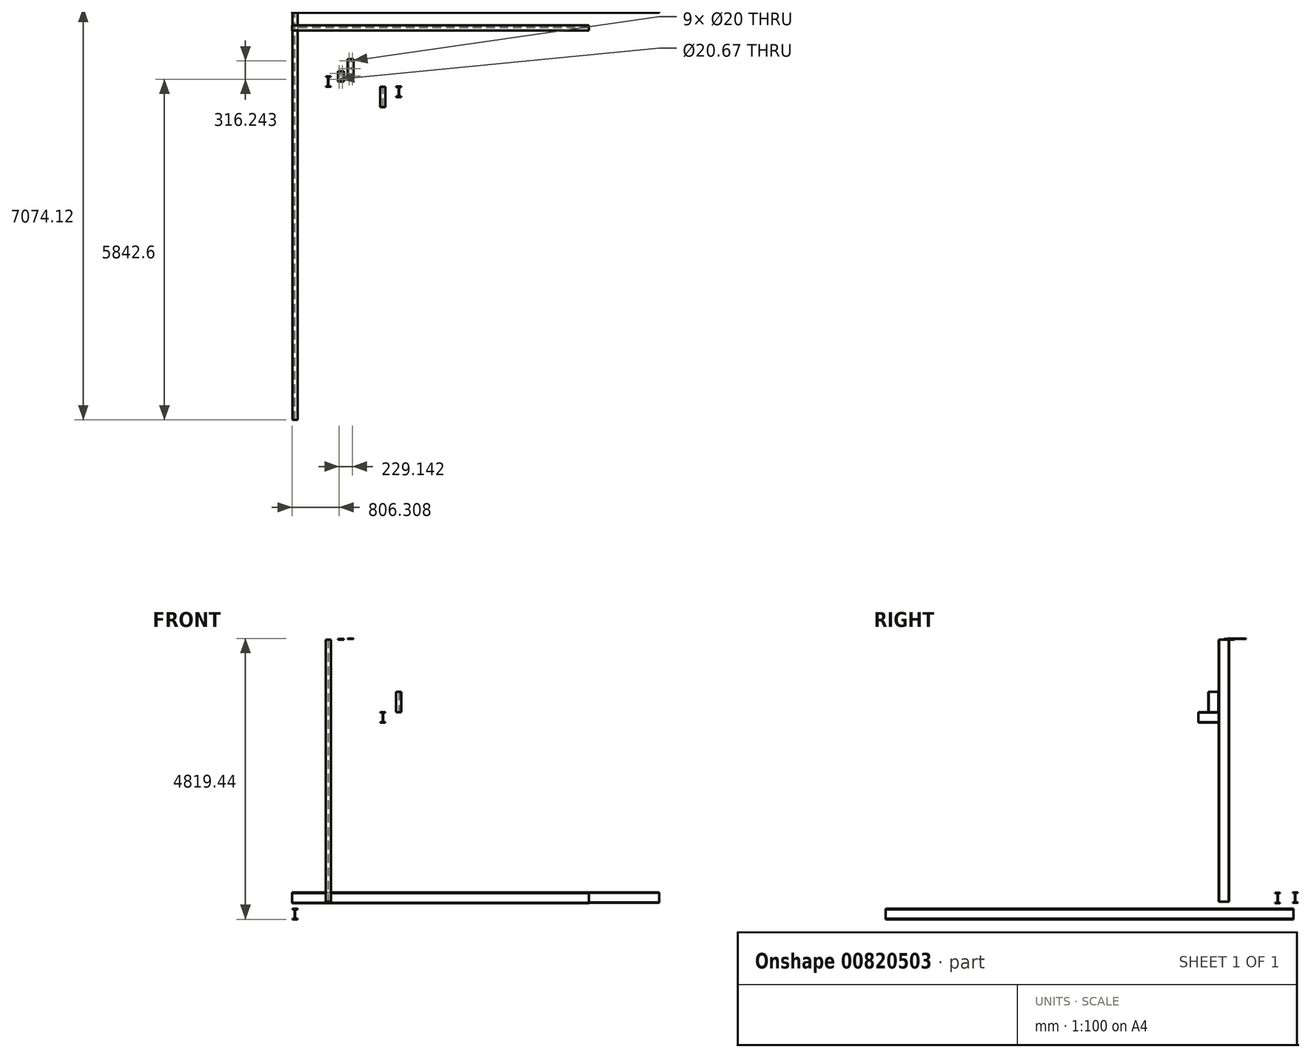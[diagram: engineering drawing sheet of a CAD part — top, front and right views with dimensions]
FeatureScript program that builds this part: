
annotation { "Feature Type Name" : "Feature", "Feature Type Description" : "" }
export const myFeature = defineFeature(function(context is Context, id is Id, definition is map)
    precondition{}
    {
        {
            var Q0;
            Q0=qCreatedBy(makeId("Right.planeOp"),FACE);
            var sketch = newSketch(context, id + "F0", { "sketchPlane" : qUnion([Q0])});
            skLineSegment(sketch, "E0", {"start": v(74.12, -15.88) * mm, "end": v(-15.88, -15.88) * mm});
            skLineSegment(sketch, "E1", {"start": v(-15.88, -15.88) * mm, "end": v(-15.88, -7.88) * mm});
            skLineSegment(sketch, "E2", {"start": v(-15.88, -7.88) * mm, "end": v(26.12, -7.88) * mm});
            skLineSegment(sketch, "E3", {"start": v(26.12, -7.88) * mm, "end": v(26.12, 156.12) * mm});
            skLineSegment(sketch, "E4", {"start": v(26.12, 156.12) * mm, "end": v(-15.88, 156.12) * mm});
            skLineSegment(sketch, "E5", {"start": v(-15.88, 156.12) * mm, "end": v(-15.88, 164.12) * mm});
            skLineSegment(sketch, "E6", {"start": v(-15.88, 164.12) * mm, "end": v(74.12, 164.12) * mm});
            skLineSegment(sketch, "E7", {"start": v(74.12, 164.12) * mm, "end": v(74.12, 156.12) * mm});
            skLineSegment(sketch, "E8", {"start": v(74.12, 156.12) * mm, "end": v(32.12, 156.12) * mm});
            skLineSegment(sketch, "E9", {"start": v(32.12, 156.12) * mm, "end": v(32.12, -7.88) * mm});
            skLineSegment(sketch, "E10", {"start": v(32.12, -7.88) * mm, "end": v(74.12, -7.88) * mm});
            skLineSegment(sketch, "E11", {"start": v(74.12, -7.88) * mm, "end": v(74.12, -15.88) * mm});
            skSolve(sketch);
        }
        {
            var Q0;
            Q0=makeQuery(id+"F0.imprint","IMPRINT",FACE,{"disambiguationData":[TD([[makeQuery(id+"F0.imprint","IMPRINT",EDGE,{"derivedFrom":sQuery(id+"F0.wireOp",EDGE,"E0")}),-1.0]])]});
            extrude(context, id + "F1", {"entities" : qUnion([Q0]), "depth" : 6300 * mm, "offsetDistance" : 25 * mm});
        }
        {
            var Q0;
            Q0=qCreatedBy(makeId("Front.planeOp"),FACE);
            var sketch = newSketch(context, id + "F2", { "sketchPlane" : qUnion([Q0])});
            skLineSegment(sketch, "E12", {"start": v(5.31, -299.44) * mm, "end": v(95.31, -299.44) * mm});
            skLineSegment(sketch, "E13", {"start": v(95.31, -299.44) * mm, "end": v(95.31, -291.44) * mm});
            skLineSegment(sketch, "E14", {"start": v(95.31, -291.44) * mm, "end": v(53.31, -291.44) * mm});
            skLineSegment(sketch, "E15", {"start": v(53.31, -291.44) * mm, "end": v(53.31, -127.44) * mm});
            skLineSegment(sketch, "E16", {"start": v(53.31, -127.44) * mm, "end": v(95.31, -127.44) * mm});
            skLineSegment(sketch, "E17", {"start": v(95.31, -127.44) * mm, "end": v(95.31, -119.44) * mm});
            skLineSegment(sketch, "E18", {"start": v(95.31, -119.44) * mm, "end": v(5.31, -119.44) * mm});
            skLineSegment(sketch, "E19", {"start": v(5.31, -119.44) * mm, "end": v(5.31, -127.44) * mm});
            skLineSegment(sketch, "E20", {"start": v(5.31, -127.44) * mm, "end": v(47.31, -127.44) * mm});
            skLineSegment(sketch, "E21", {"start": v(47.31, -127.44) * mm, "end": v(47.31, -291.44) * mm});
            skLineSegment(sketch, "E22", {"start": v(47.31, -291.44) * mm, "end": v(5.31, -291.44) * mm});
            skLineSegment(sketch, "E23", {"start": v(5.31, -291.44) * mm, "end": v(5.31, -299.44) * mm});
            skSolve(sketch);
        }
        {
            var Q0;
            Q0=makeQuery(id+"F2.imprint","IMPRINT",FACE,{"disambiguationData":[TD([[makeQuery(id+"F2.imprint","IMPRINT",EDGE,{"derivedFrom":sQuery(id+"F2.wireOp",EDGE,"E12")}),1.0]])]});
            extrude(context, id + "F3", {"entities" : qUnion([Q0]), "depth" : 7000 * mm, "offsetDistance" : 25 * mm});
        }
        {
            var Q0;
            Q0=qCreatedBy(makeId("Right.planeOp"),FACE);
            var sketch = newSketch(context, id + "F4", { "sketchPlane" : qUnion([Q0])});
            skLineSegment(sketch, "E24", {"start": v(-227.32, -23.27) * mm, "end": v(-317.32, -23.27) * mm});
            skLineSegment(sketch, "E25", {"start": v(-317.32, -23.27) * mm, "end": v(-317.32, -15.27) * mm});
            skLineSegment(sketch, "E26", {"start": v(-317.32, -15.27) * mm, "end": v(-275.32, -15.27) * mm});
            skLineSegment(sketch, "E27", {"start": v(-275.32, -15.27) * mm, "end": v(-275.32, 148.73) * mm});
            skLineSegment(sketch, "E28", {"start": v(-275.32, 148.73) * mm, "end": v(-317.32, 148.73) * mm});
            skLineSegment(sketch, "E29", {"start": v(-317.32, 148.73) * mm, "end": v(-317.32, 156.73) * mm});
            skLineSegment(sketch, "E30", {"start": v(-317.32, 156.73) * mm, "end": v(-227.32, 156.73) * mm});
            skLineSegment(sketch, "E31", {"start": v(-227.32, 156.73) * mm, "end": v(-227.32, 148.73) * mm});
            skLineSegment(sketch, "E32", {"start": v(-227.32, 148.73) * mm, "end": v(-269.32, 148.73) * mm});
            skLineSegment(sketch, "E33", {"start": v(-269.32, 148.73) * mm, "end": v(-269.32, -15.27) * mm});
            skLineSegment(sketch, "E34", {"start": v(-269.32, -15.27) * mm, "end": v(-227.32, -15.27) * mm});
            skLineSegment(sketch, "E35", {"start": v(-227.32, -15.27) * mm, "end": v(-227.32, -23.27) * mm});
            skSolve(sketch);
        }
        {
            var Q0;
            Q0=makeQuery(id+"F4.imprint","IMPRINT",FACE,{"disambiguationData":[TD([[makeQuery(id+"F4.imprint","IMPRINT",EDGE,{"derivedFrom":sQuery(id+"F4.wireOp",EDGE,"E24")}),-1.0]])]});
            extrude(context, id + "F5", {"entities" : qUnion([Q0]), "depth" : 5090 * mm, "offsetDistance" : 25 * mm});
        }
        {
            var Q0;
            Q0=qCreatedBy(makeId("Top.planeOp"),FACE);
            var sketch = newSketch(context, id + "F6", { "sketchPlane" : qUnion([Q0])});
            skLineSegment(sketch, "E36", {"start": v(574.81, -1284.27) * mm, "end": v(664.81, -1284.27) * mm});
            skLineSegment(sketch, "E37", {"start": v(664.81, -1284.27) * mm, "end": v(664.81, -1276.27) * mm});
            skLineSegment(sketch, "E38", {"start": v(664.81, -1276.27) * mm, "end": v(622.81, -1276.27) * mm});
            skLineSegment(sketch, "E39", {"start": v(622.81, -1276.27) * mm, "end": v(622.81, -1112.27) * mm});
            skLineSegment(sketch, "E40", {"start": v(622.81, -1112.27) * mm, "end": v(664.81, -1112.27) * mm});
            skLineSegment(sketch, "E41", {"start": v(664.81, -1112.27) * mm, "end": v(664.81, -1104.27) * mm});
            skLineSegment(sketch, "E42", {"start": v(664.81, -1104.27) * mm, "end": v(574.81, -1104.27) * mm});
            skLineSegment(sketch, "E43", {"start": v(574.81, -1104.27) * mm, "end": v(574.81, -1112.27) * mm});
            skLineSegment(sketch, "E44", {"start": v(574.81, -1112.27) * mm, "end": v(616.81, -1112.27) * mm});
            skLineSegment(sketch, "E45", {"start": v(616.81, -1112.27) * mm, "end": v(616.81, -1276.27) * mm});
            skLineSegment(sketch, "E46", {"start": v(616.81, -1276.27) * mm, "end": v(574.81, -1276.27) * mm});
            skLineSegment(sketch, "E47", {"start": v(574.81, -1276.27) * mm, "end": v(574.81, -1284.27) * mm});
            skSolve(sketch);
        }
        {
            var Q0;
            Q0=makeQuery(id+"F6.imprint","IMPRINT",FACE,{"disambiguationData":[TD([[makeQuery(id+"F6.imprint","IMPRINT",EDGE,{"derivedFrom":sQuery(id+"F6.wireOp",EDGE,"E36")}),1.0]])]});
            extrude(context, id + "F7", {"entities" : qUnion([Q0]), "depth" : 4500 * mm, "offsetDistance" : 25 * mm});
        }
        {
            var Q0;
            Q0=makeQuery(id+"F7.opExtrude","CAP_FACE",FACE,{"disambiguationData":[OSD([sQuery(id+"F6.wireOp",EDGE,"E36"),sQuery(id+"F6.wireOp",EDGE,"E37"),sQuery(id+"F6.wireOp",EDGE,"E38"),sQuery(id+"F6.wireOp",EDGE,"E39"),sQuery(id+"F6.wireOp",EDGE,"E40"),sQuery(id+"F6.wireOp",EDGE,"E41"),sQuery(id+"F6.wireOp",EDGE,"E42"),sQuery(id+"F6.wireOp",EDGE,"E43"),sQuery(id+"F6.wireOp",EDGE,"E44"),sQuery(id+"F6.wireOp",EDGE,"E45"),sQuery(id+"F6.wireOp",EDGE,"E46"),sQuery(id+"F6.wireOp",EDGE,"E47")])],"isStart":false});
            var sketch = newSketch(context, id + "F8", { "sketchPlane" : qUnion([Q0])});
            skLineSegment(sketch, "E48.bottom", {"start": v(886.3, -1197.4) * mm, "end": v(786.3, -1197.4) * mm});
            skLineSegment(sketch, "E48.top", {"start": v(886.3, -1017.4) * mm, "end": v(786.3, -1017.4) * mm});
            skLineSegment(sketch, "E48.left", {"start": v(886.3, -1197.4) * mm, "end": v(886.3, -1017.4) * mm});
            skLineSegment(sketch, "E48.right", {"start": v(786.3, -1197.4) * mm, "end": v(786.3, -1017.4) * mm});
            skPoint(sketch, "E48.middle", {"position": v(836.3, -1107.4) * mm});
            skCircle(sketch, "E49", {"center": v(866.3, -1057.4) * mm, "radius": 10 * mm});
            skCircle(sketch, "E50", {"center": v(866.3, -1157.4) * mm, "radius": 10 * mm});
            skCircle(sketch, "E51", {"center": v(806.3, -1057.4) * mm, "radius": 10 * mm});
            skCircle(sketch, "E52", {"center": v(806.3, -1157.4) * mm, "radius": 10.34 * mm});
            skSolve(sketch);
        }
        {
            var Q0;
            Q0=makeQuery(id+"F8.imprint","IMPRINT",FACE,{"disambiguationData":[TD([[makeQuery(id+"F8.imprint","IMPRINT",EDGE,{"derivedFrom":sQuery(id+"F8.wireOp",EDGE,"E48.bottom")}),-1.0]])]});
            extrude(context, id + "F9", {"entities" : qUnion([Q0]), "depth" : 10 * mm, "offsetDistance" : 25 * mm});
        }
        {
            var Q0;
            Q0=makeQuery(id+"F9.opExtrude","CAP_FACE",FACE,{"disambiguationData":[OSD([sQuery(id+"F8.wireOp",EDGE,"E48.bottom"),sQuery(id+"F8.wireOp",EDGE,"E48.top"),sQuery(id+"F8.wireOp",EDGE,"E48.left"),sQuery(id+"F8.wireOp",EDGE,"E48.right"),sQuery(id+"F8.wireOp",EDGE,"E49"),sQuery(id+"F8.wireOp",EDGE,"E50"),sQuery(id+"F8.wireOp",EDGE,"E51"),sQuery(id+"F8.wireOp",EDGE,"E52")])],"isStart":false});
            var sketch = newSketch(context, id + "F10", { "sketchPlane" : qUnion([Q0])});
            skLineSegment(sketch, "E53.bottom", {"start": v(1055.45, -1131.16) * mm, "end": v(955.45, -1131.16) * mm});
            skLineSegment(sketch, "E53.top", {"start": v(1055.45, -811.16) * mm, "end": v(955.45, -811.16) * mm});
            skLineSegment(sketch, "E53.left", {"start": v(1055.45, -1131.16) * mm, "end": v(1055.45, -811.16) * mm});
            skLineSegment(sketch, "E53.right", {"start": v(955.45, -1131.16) * mm, "end": v(955.45, -811.16) * mm});
            skPoint(sketch, "E53.middle", {"position": v(1005.45, -971.16) * mm});
            skCircle(sketch, "E54", {"center": v(1035.45, -841.16) * mm, "radius": 10 * mm});
            skCircle(sketch, "E55", {"center": v(1035.45, -971.16) * mm, "radius": 10 * mm});
            skCircle(sketch, "E56", {"center": v(1035.45, -1101.16) * mm, "radius": 10 * mm});
            skCircle(sketch, "E57", {"center": v(975.45, -841.16) * mm, "radius": 10 * mm});
            skCircle(sketch, "E58", {"center": v(975.45, -971.16) * mm, "radius": 10 * mm});
            skCircle(sketch, "E59", {"center": v(975.45, -1101.16) * mm, "radius": 10 * mm});
            skSolve(sketch);
        }
        {
            var Q0;
            Q0=makeQuery(id+"F10.imprint","IMPRINT",FACE,{"disambiguationData":[TD([[makeQuery(id+"F10.imprint","IMPRINT",EDGE,{"derivedFrom":sQuery(id+"F10.wireOp",EDGE,"E53.bottom")}),-1.0]])]});
            extrude(context, id + "F11", {"entities" : qUnion([Q0]), "depth" : 10 * mm, "offsetDistance" : 25 * mm});
        }
        {
            var Q0;
            Q0=makeQuery(id+"F7.opExtrude","SWEPT_FACE",FACE,{"disambiguationData":[OSD([sQuery(id+"F6.wireOp",EDGE,"E36")])]});
            var sketch = newSketch(context, id + "F12", { "sketchPlane" : qUnion([Q0])});
            skLineSegment(sketch, "E60", {"start": v(1511.13, 3076.07) * mm, "end": v(1601.13, 3076.07) * mm});
            skLineSegment(sketch, "E61", {"start": v(1601.13, 3076.07) * mm, "end": v(1601.13, 3084.07) * mm});
            skLineSegment(sketch, "E62", {"start": v(1601.13, 3084.07) * mm, "end": v(1559.13, 3084.07) * mm});
            skLineSegment(sketch, "E63", {"start": v(1559.13, 3084.07) * mm, "end": v(1559.13, 3248.07) * mm});
            skLineSegment(sketch, "E64", {"start": v(1559.13, 3248.07) * mm, "end": v(1601.13, 3248.07) * mm});
            skLineSegment(sketch, "E65", {"start": v(1601.13, 3248.07) * mm, "end": v(1601.13, 3256.07) * mm});
            skLineSegment(sketch, "E66", {"start": v(1601.13, 3256.07) * mm, "end": v(1511.13, 3256.07) * mm});
            skLineSegment(sketch, "E67", {"start": v(1511.13, 3256.07) * mm, "end": v(1511.13, 3248.07) * mm});
            skLineSegment(sketch, "E68", {"start": v(1511.13, 3248.07) * mm, "end": v(1553.13, 3248.07) * mm});
            skLineSegment(sketch, "E69", {"start": v(1553.13, 3248.07) * mm, "end": v(1553.13, 3084.07) * mm});
            skLineSegment(sketch, "E70", {"start": v(1553.13, 3084.07) * mm, "end": v(1511.13, 3084.07) * mm});
            skLineSegment(sketch, "E71", {"start": v(1511.13, 3084.07) * mm, "end": v(1511.13, 3076.07) * mm});
            skSolve(sketch);
        }
        {
            var Q0;
            Q0=makeQuery(id+"F12.imprint","IMPRINT",FACE,{"disambiguationData":[TD([[makeQuery(id+"F12.imprint","IMPRINT",EDGE,{"derivedFrom":sQuery(id+"F12.wireOp",EDGE,"E60")}),1.0]])]});
            extrude(context, id + "F13", {"entities" : qUnion([Q0]), "depth" : 350 * mm, "offsetDistance" : 25 * mm});
        }
        {
            var Q0;
            Q0=makeQuery(id+"F13.opExtrude","SWEPT_FACE",FACE,{"disambiguationData":[OSD([sQuery(id+"F12.wireOp",EDGE,"E66")])]});
            var sketch = newSketch(context, id + "F14", { "sketchPlane" : qUnion([Q0])});
            skLineSegment(sketch, "E72", {"start": v(1784.05, -1280.2) * mm, "end": v(1874.05, -1280.2) * mm});
            skLineSegment(sketch, "E73", {"start": v(1874.05, -1280.2) * mm, "end": v(1874.05, -1288.2) * mm});
            skLineSegment(sketch, "E74", {"start": v(1874.05, -1288.2) * mm, "end": v(1832.05, -1288.2) * mm});
            skLineSegment(sketch, "E75", {"start": v(1832.05, -1288.2) * mm, "end": v(1832.05, -1452.2) * mm});
            skLineSegment(sketch, "E76", {"start": v(1832.05, -1452.2) * mm, "end": v(1874.05, -1452.2) * mm});
            skLineSegment(sketch, "E77", {"start": v(1874.05, -1452.2) * mm, "end": v(1874.05, -1460.2) * mm});
            skLineSegment(sketch, "E78", {"start": v(1874.05, -1460.2) * mm, "end": v(1784.05, -1460.2) * mm});
            skLineSegment(sketch, "E79", {"start": v(1784.05, -1460.2) * mm, "end": v(1784.05, -1452.2) * mm});
            skLineSegment(sketch, "E80", {"start": v(1784.05, -1452.2) * mm, "end": v(1826.05, -1452.2) * mm});
            skLineSegment(sketch, "E81", {"start": v(1826.05, -1452.2) * mm, "end": v(1826.05, -1288.2) * mm});
            skLineSegment(sketch, "E82", {"start": v(1826.05, -1288.2) * mm, "end": v(1784.05, -1288.2) * mm});
            skLineSegment(sketch, "E83", {"start": v(1784.05, -1288.2) * mm, "end": v(1784.05, -1280.2) * mm});
            skSolve(sketch);
        }
        {
            var Q0;
            Q0=makeQuery(id+"F14.imprint","IMPRINT",FACE,{"disambiguationData":[TD([[makeQuery(id+"F14.imprint","IMPRINT",EDGE,{"derivedFrom":sQuery(id+"F14.wireOp",EDGE,"E72")}),-1.0]])]});
            extrude(context, id + "F15", {"entities" : qUnion([Q0]), "depth" : 350 * mm, "offsetDistance" : 25 * mm});
        }
    });
